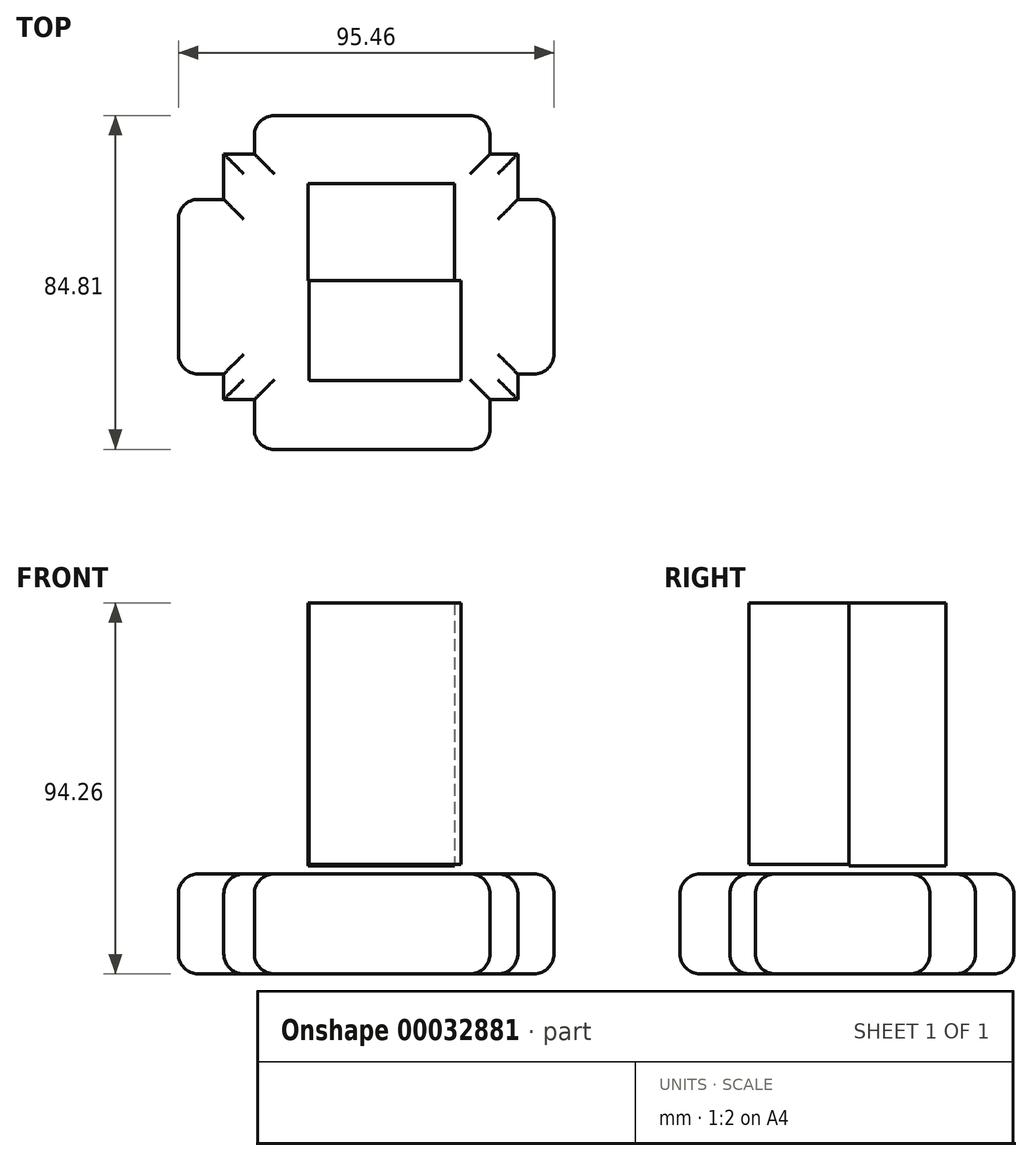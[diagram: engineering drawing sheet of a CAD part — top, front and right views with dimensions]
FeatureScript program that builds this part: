
annotation { "Feature Type Name" : "Feature", "Feature Type Description" : "" }
export const myFeature = defineFeature(function(context is Context, id is Id, definition is map)
    precondition{}
    {
        {
            var Q0;
            Q0=qCreatedBy(makeId("Top.planeOp"),FACE);
            var sketch = newSketch(context, id + "F0", { "sketchPlane" : qUnion([Q0])});
            skLineSegment(sketch, "E0.bottom", {"start": v(-35.73, 32.12) * mm, "end": v(38.98, 32.12) * mm});
            skLineSegment(sketch, "E0.top", {"start": v(-35.73, -30.31) * mm, "end": v(38.98, -30.31) * mm});
            skLineSegment(sketch, "E0.left", {"start": v(-35.73, 32.12) * mm, "end": v(-35.73, -30.31) * mm});
            skLineSegment(sketch, "E0.right", {"start": v(38.98, 32.12) * mm, "end": v(38.98, -30.31) * mm});
            skLineSegment(sketch, "E1.bottom", {"start": v(31.94, 41.86) * mm, "end": v(-27.97, 41.86) * mm});
            skLineSegment(sketch, "E1.top", {"start": v(31.94, -42.95) * mm, "end": v(-27.97, -42.95) * mm});
            skLineSegment(sketch, "E1.left", {"start": v(31.94, 41.86) * mm, "end": v(31.94, -42.95) * mm});
            skLineSegment(sketch, "E1.right", {"start": v(-27.97, 41.86) * mm, "end": v(-27.97, -42.95) * mm});
            skLineSegment(sketch, "E2.bottom", {"start": v(-47.28, 20.57) * mm, "end": v(48.18, 20.57) * mm});
            skLineSegment(sketch, "E2.top", {"start": v(-47.28, -23.82) * mm, "end": v(48.18, -23.82) * mm});
            skLineSegment(sketch, "E2.left", {"start": v(-47.28, 20.57) * mm, "end": v(-47.28, -23.82) * mm});
            skLineSegment(sketch, "E2.right", {"start": v(48.18, 20.57) * mm, "end": v(48.18, -23.82) * mm});
            skSolve(sketch);
        }
        {
            var Q0;
            {var subQ3=sQuery(id+"F0.wireOp",EDGE,"E1.left");var subQ5=sQuery(id+"F0.wireOp",EDGE,"E2.bottom");var subQ7=makeQuery(id+"F0.imprint","INTERSECT",VERTEX,{"derivedFrom":[subQ3,subQ5]});Q0=makeQuery(id+"F0.imprint","IMPRINT",FACE,{"disambiguationData":[TD([[makeQuery(id+"F0.imprint","IMPRINT",EDGE,{"disambiguationData":[TD([[subQ7,-1.0]])],"derivedFrom":subQ3}),-1.0]])]});}
            var Q1;
            {var subQ1=sQuery(id+"F0.wireOp",EDGE,"E1.right");var subQ5=sQuery(id+"F0.wireOp",EDGE,"E0.bottom");var subQ6=makeQuery(id+"F0.imprint","INTERSECT",VERTEX,{"derivedFrom":[subQ5,subQ1]});Q1=makeQuery(id+"F0.imprint","IMPRINT",FACE,{"disambiguationData":[TD([[makeQuery(id+"F0.imprint","IMPRINT",EDGE,{"disambiguationData":[TD([[subQ6,-1.0]])],"derivedFrom":subQ5}),-1.0]])]});}
            var Q2;
            {var subQ3=sQuery(id+"F0.wireOp",EDGE,"E1.bottom");Q2=makeQuery(id+"F0.imprint","IMPRINT",FACE,{"disambiguationData":[TD([[makeQuery(id+"F0.imprint","IMPRINT",EDGE,{"derivedFrom":subQ3}),1.0]])]});}
            var Q3;
            {var subQ0=sQuery(id+"F0.wireOp",EDGE,"E2.left");Q3=makeQuery(id+"F0.imprint","IMPRINT",FACE,{"disambiguationData":[TD([[makeQuery(id+"F0.imprint","IMPRINT",EDGE,{"derivedFrom":subQ0}),1.0]])]});}
            var Q4;
            {var subQ3=sQuery(id+"F0.wireOp",EDGE,"E0.left");var subQ5=sQuery(id+"F0.wireOp",EDGE,"E0.bottom");var subQ7=makeQuery(id+"F0.imprint","INTERSECT",VERTEX,{"derivedFrom":[subQ5,subQ3]});Q4=makeQuery(id+"F0.imprint","IMPRINT",FACE,{"disambiguationData":[TD([[makeQuery(id+"F0.imprint","IMPRINT",EDGE,{"disambiguationData":[TD([[subQ7,-1.0]])],"derivedFrom":subQ5}),-1.0]])]});}
            var Q5;
            {var subQ3=sQuery(id+"F0.wireOp",EDGE,"E0.left");var subQ5=sQuery(id+"F0.wireOp",EDGE,"E2.bottom");var subQ7=makeQuery(id+"F0.imprint","INTERSECT",VERTEX,{"derivedFrom":[subQ3,subQ5]});Q5=makeQuery(id+"F0.imprint","IMPRINT",FACE,{"disambiguationData":[TD([[makeQuery(id+"F0.imprint","IMPRINT",EDGE,{"disambiguationData":[TD([[subQ7,-1.0]])],"derivedFrom":subQ3}),1.0]])]});}
            var Q6;
            {var subQ1=sQuery(id+"F0.wireOp",EDGE,"E1.right");var subQ5=sQuery(id+"F0.wireOp",EDGE,"E0.top");var subQ6=makeQuery(id+"F0.imprint","INTERSECT",VERTEX,{"derivedFrom":[subQ5,subQ1]});Q6=makeQuery(id+"F0.imprint","IMPRINT",FACE,{"disambiguationData":[TD([[makeQuery(id+"F0.imprint","IMPRINT",EDGE,{"disambiguationData":[TD([[subQ6,-1.0]])],"derivedFrom":subQ5}),1.0]])]});}
            var Q7;
            {var subQ3=sQuery(id+"F0.wireOp",EDGE,"E1.top");Q7=makeQuery(id+"F0.imprint","IMPRINT",FACE,{"disambiguationData":[TD([[makeQuery(id+"F0.imprint","IMPRINT",EDGE,{"derivedFrom":subQ3}),-1.0]])]});}
            var Q8;
            {var subQ3=sQuery(id+"F0.wireOp",EDGE,"E0.left");var subQ5=sQuery(id+"F0.wireOp",EDGE,"E0.top");var subQ7=makeQuery(id+"F0.imprint","INTERSECT",VERTEX,{"derivedFrom":[subQ5,subQ3]});Q8=makeQuery(id+"F0.imprint","IMPRINT",FACE,{"disambiguationData":[TD([[makeQuery(id+"F0.imprint","IMPRINT",EDGE,{"disambiguationData":[TD([[subQ7,-1.0]])],"derivedFrom":subQ5}),1.0]])]});}
            var Q9;
            {var subQ3=sQuery(id+"F0.wireOp",EDGE,"E2.right");Q9=makeQuery(id+"F0.imprint","IMPRINT",FACE,{"disambiguationData":[TD([[makeQuery(id+"F0.imprint","IMPRINT",EDGE,{"derivedFrom":subQ3}),-1.0]])]});}
            var Q10;
            {var subQ3=sQuery(id+"F0.wireOp",EDGE,"E0.right");var subQ5=sQuery(id+"F0.wireOp",EDGE,"E0.bottom");var subQ7=makeQuery(id+"F0.imprint","INTERSECT",VERTEX,{"derivedFrom":[subQ5,subQ3]});Q10=makeQuery(id+"F0.imprint","IMPRINT",FACE,{"disambiguationData":[TD([[makeQuery(id+"F0.imprint","IMPRINT",EDGE,{"disambiguationData":[TD([[subQ7,1.0]])],"derivedFrom":subQ5}),-1.0]])]});}
            var Q11;
            {var subQ3=sQuery(id+"F0.wireOp",EDGE,"E0.right");var subQ5=sQuery(id+"F0.wireOp",EDGE,"E0.top");var subQ7=makeQuery(id+"F0.imprint","INTERSECT",VERTEX,{"derivedFrom":[subQ5,subQ3]});Q11=makeQuery(id+"F0.imprint","IMPRINT",FACE,{"disambiguationData":[TD([[makeQuery(id+"F0.imprint","IMPRINT",EDGE,{"disambiguationData":[TD([[subQ7,1.0]])],"derivedFrom":subQ5}),1.0]])]});}
            var Q12;
            {var subQ3=sQuery(id+"F0.wireOp",EDGE,"E0.right");var subQ5=sQuery(id+"F0.wireOp",EDGE,"E2.bottom");var subQ7=makeQuery(id+"F0.imprint","INTERSECT",VERTEX,{"derivedFrom":[subQ3,subQ5]});Q12=makeQuery(id+"F0.imprint","IMPRINT",FACE,{"disambiguationData":[TD([[makeQuery(id+"F0.imprint","IMPRINT",EDGE,{"disambiguationData":[TD([[subQ7,-1.0]])],"derivedFrom":subQ3}),-1.0]])]});}
            extrude(context, id + "F1", {"entities" : qUnion([Q0, Q1, Q2, Q3, Q4, Q5, Q6, Q7, Q8, Q9, Q10, Q11, Q12]), "depth" : 25.4 * mm});
        }
        {
            var Q0;
            Q0=makeQuery(id+"F1.opExtrude","CAP_FACE",FACE,{"disambiguationData":[OSD([sQuery(id+"F0.wireOp",EDGE,"E0.bottom"),sQuery(id+"F0.wireOp",EDGE,"E0.top"),sQuery(id+"F0.wireOp",EDGE,"E0.left"),sQuery(id+"F0.wireOp",EDGE,"E0.right"),sQuery(id+"F0.wireOp",EDGE,"E1.bottom"),sQuery(id+"F0.wireOp",EDGE,"E1.top"),sQuery(id+"F0.wireOp",EDGE,"E1.left"),sQuery(id+"F0.wireOp",EDGE,"E1.right"),sQuery(id+"F0.wireOp",EDGE,"E2.bottom"),sQuery(id+"F0.wireOp",EDGE,"E2.top"),sQuery(id+"F0.wireOp",EDGE,"E2.left"),sQuery(id+"F0.wireOp",EDGE,"E2.right")])],"isStart":false});
            var Q1;
            Q1=makeQuery(id+"F1.opExtrude","CAP_FACE",FACE,{"disambiguationData":[OSD([sQuery(id+"F0.wireOp",EDGE,"E0.bottom"),sQuery(id+"F0.wireOp",EDGE,"E0.top"),sQuery(id+"F0.wireOp",EDGE,"E0.left"),sQuery(id+"F0.wireOp",EDGE,"E0.right"),sQuery(id+"F0.wireOp",EDGE,"E1.bottom"),sQuery(id+"F0.wireOp",EDGE,"E1.top"),sQuery(id+"F0.wireOp",EDGE,"E1.left"),sQuery(id+"F0.wireOp",EDGE,"E1.right"),sQuery(id+"F0.wireOp",EDGE,"E2.bottom"),sQuery(id+"F0.wireOp",EDGE,"E2.top"),sQuery(id+"F0.wireOp",EDGE,"E2.left"),sQuery(id+"F0.wireOp",EDGE,"E2.right")])],"isStart":true});
            var Q2;
            Q2=makeQuery(id+"F1.opExtrude","SWEPT_FACE",FACE,{"disambiguationData":[OSD([sQuery(id+"F0.wireOp",EDGE,"E1.top")])]});
            var Q3;
            Q3=makeQuery(id+"F1.opExtrude","SWEPT_FACE",FACE,{"disambiguationData":[OSD([sQuery(id+"F0.wireOp",EDGE,"E2.left")])]});
            var Q4;
            Q4=makeQuery(id+"F1.opExtrude","SWEPT_FACE",FACE,{"disambiguationData":[OSD([sQuery(id+"F0.wireOp",EDGE,"E1.bottom")])]});
            var Q5;
            Q5=makeQuery(id+"F1.opExtrude","SWEPT_FACE",FACE,{"disambiguationData":[OSD([sQuery(id+"F0.wireOp",EDGE,"E2.right")])]});
            fillet(context, id + "F2", {"entities" : qUnion([Q0, Q1, Q2, Q3, Q4, Q5]), "radius" : 5.08 * mm, "tangentPropagation" : true, "allowEdgeOverflow" : false});
        }
        {
            var Q0;
            Q0=qCreatedBy(makeId("Front.planeOp"),FACE);
            var sketch = newSketch(context, id + "F3", { "sketchPlane" : qUnion([Q0])});
            skLineSegment(sketch, "E3.bottom", {"start": v(-14.07, 27.79) * mm, "end": v(24.54, 27.79) * mm});
            skLineSegment(sketch, "E3.top", {"start": v(-14.07, 94.2) * mm, "end": v(24.54, 94.2) * mm});
            skLineSegment(sketch, "E3.left", {"start": v(-14.07, 27.79) * mm, "end": v(-14.07, 94.2) * mm});
            skLineSegment(sketch, "E3.right", {"start": v(24.54, 27.79) * mm, "end": v(24.54, 94.2) * mm});
            skSolve(sketch);
        }
        {
            var Q0;
            Q0=makeQuery(id+"F3.imprint","IMPRINT",FACE,{"disambiguationData":[TD([[makeQuery(id+"F3.imprint","IMPRINT",EDGE,{"derivedFrom":sQuery(id+"F3.wireOp",EDGE,"E3.bottom")}),1.0]])]});
            extrude(context, id + "F4", {"entities" : qUnion([Q0]), "depth" : 25.4 * mm});
        }
        {
            var Q0;
            Q0=qCreatedBy(makeId("Front.planeOp"),FACE);
            var sketch = newSketch(context, id + "F5", { "sketchPlane" : qUnion([Q0])});
            skLineSegment(sketch, "E4.bottom", {"start": v(22.91, 94.26) * mm, "end": v(-14.27, 94.26) * mm});
            skLineSegment(sketch, "E4.top", {"start": v(22.91, 27.4) * mm, "end": v(-14.27, 27.4) * mm});
            skLineSegment(sketch, "E4.left", {"start": v(22.91, 94.26) * mm, "end": v(22.91, 27.4) * mm});
            skLineSegment(sketch, "E4.right", {"start": v(-14.27, 94.26) * mm, "end": v(-14.27, 27.4) * mm});
            skSolve(sketch);
        }
        {
            var Q0;
            Q0=makeQuery(id+"F5.imprint","IMPRINT",FACE,{"disambiguationData":[TD([[makeQuery(id+"F5.imprint","IMPRINT",EDGE,{"derivedFrom":sQuery(id+"F5.wireOp",EDGE,"E4.bottom")}),1.0]])]});
            extrude(context, id + "F6", {"entities" : qUnion([Q0]), "operationType" : NewBodyOperationType.ADD, "oppositeDirection" : true, "depth" : 24.65 * mm});
        }
    });
